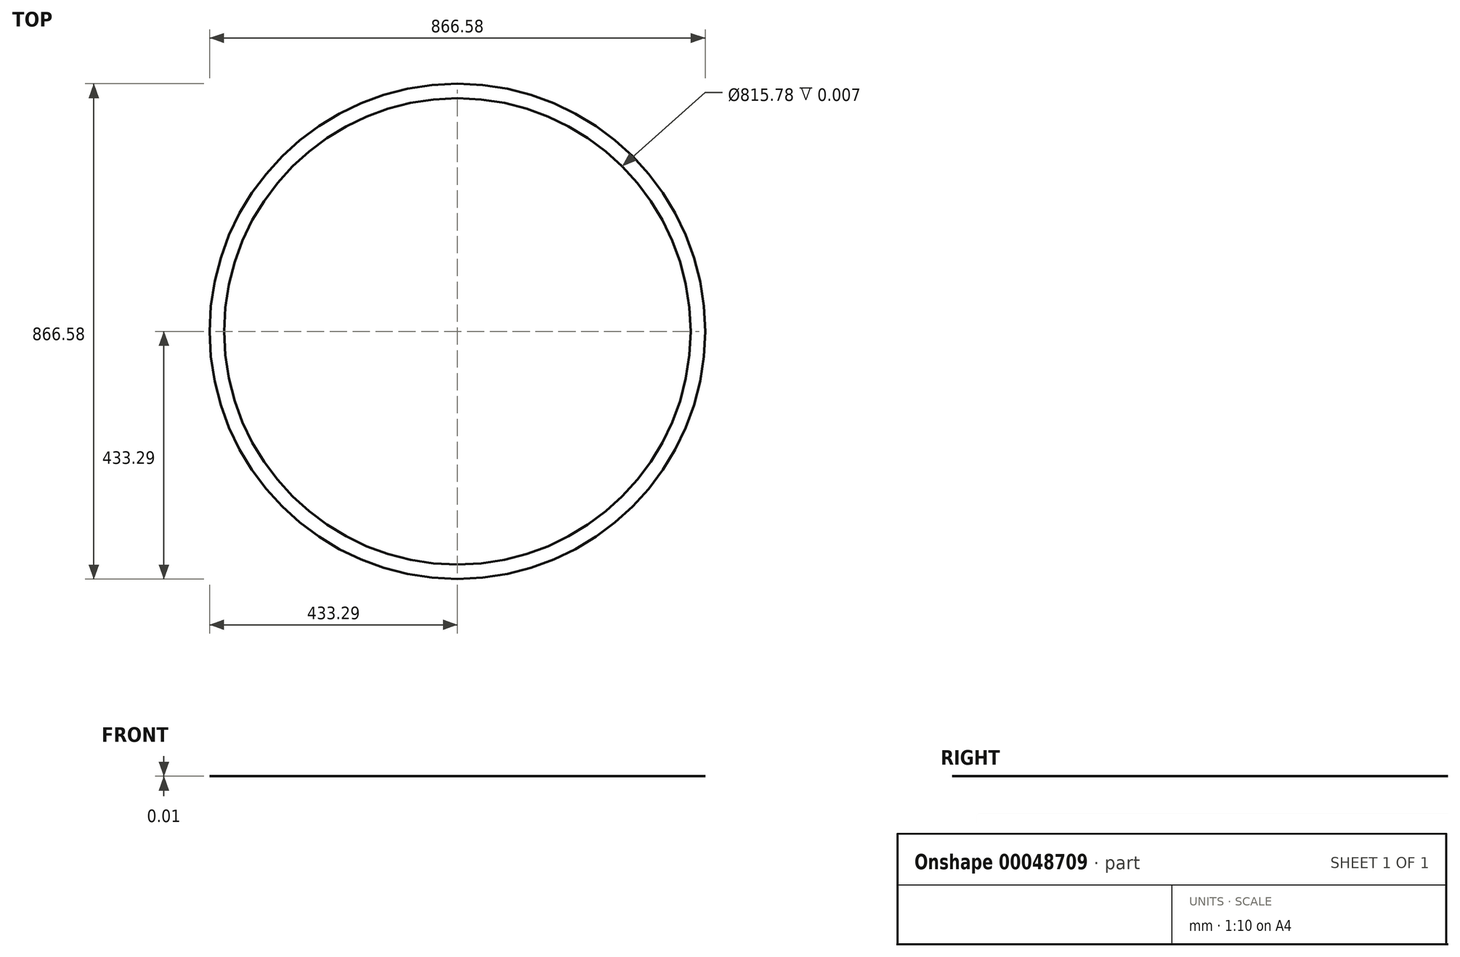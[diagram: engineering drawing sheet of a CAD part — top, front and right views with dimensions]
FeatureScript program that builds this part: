
annotation { "Feature Type Name" : "Feature", "Feature Type Description" : "" }
export const myFeature = defineFeature(function(context is Context, id is Id, definition is map)
    precondition{}
    {
        {
            var Q0;
            Q0=qCreatedBy(makeId("Top.planeOp"),FACE);
            var sketch = newSketch(context, id + "F0", { "sketchPlane" : qUnion([Q0])});
            skCircle(sketch, "E0", {"center": v(0, 0) * mm, "radius": 433.3 * mm});
            skCircle(sketch, "E1", {"center": v(0, 0) * mm, "radius": 407.9 * mm});
            skSolve(sketch);
        }
        {
            var Q0;
            Q0 = qSketchRegion(id + "F0", true);
            extrude(context, id + "F1", {"entities" : qUnion([Q0]), "depth" : 3 / 457.2 * mm});
        }
    });
